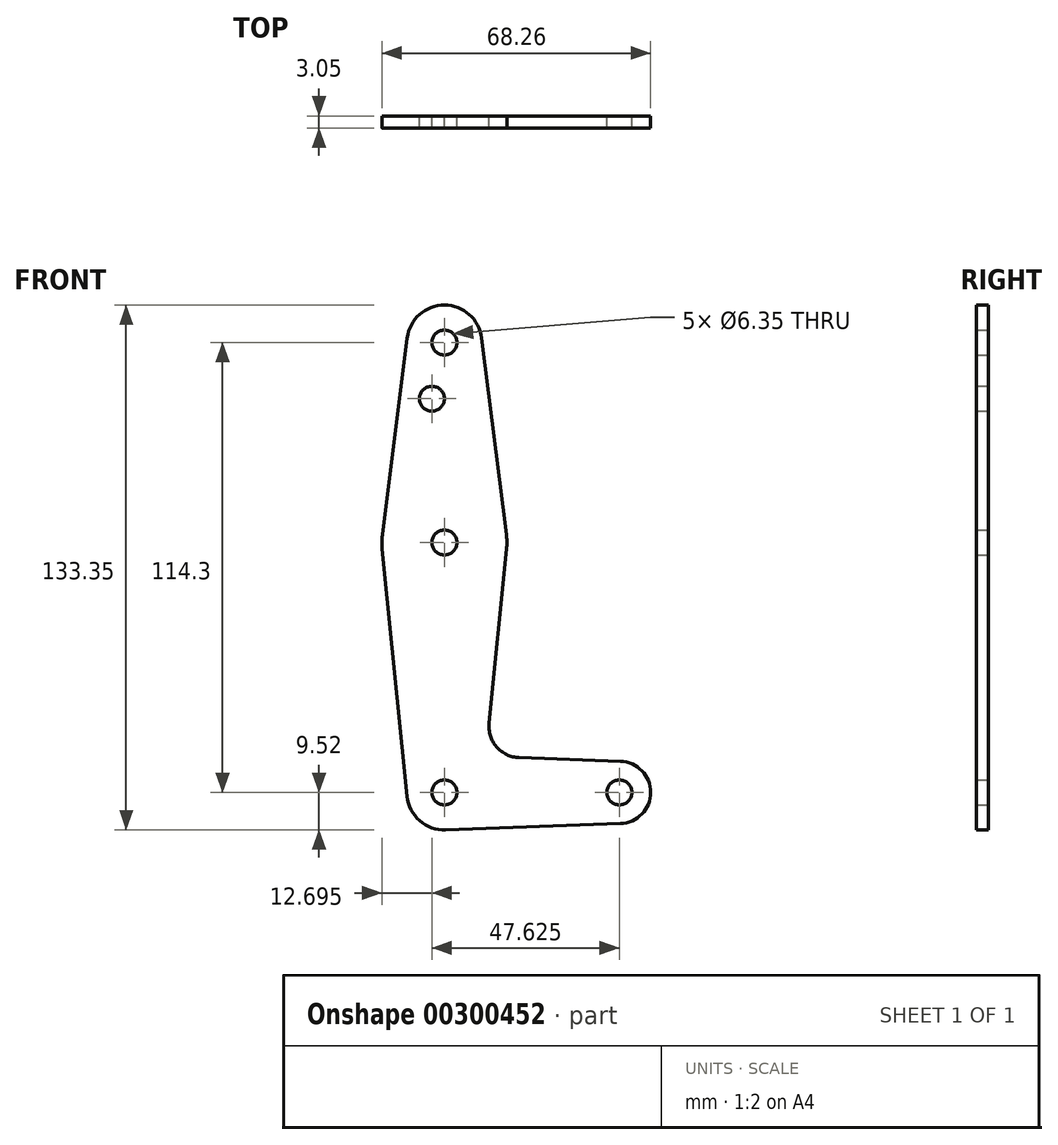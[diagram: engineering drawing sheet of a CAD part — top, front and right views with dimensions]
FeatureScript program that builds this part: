
annotation { "Feature Type Name" : "Feature", "Feature Type Description" : "" }
export const myFeature = defineFeature(function(context is Context, id is Id, definition is map)
    precondition{}
    {
        {
            var Q0;
            Q0=qCreatedBy(makeId("Front.planeOp"),FACE);
            var sketch = newSketch(context, id + "F0", { "sketchPlane" : qUnion([Q0])});
            skLineSegment(sketch, "E0", {"start": v(0, 114.3) * mm, "end": v(0, 0) * mm, "construction": true});
            skLineSegment(sketch, "E1", {"start": v(0, 0) * mm, "end": v(44.45, 0) * mm, "construction": true});
            skCircle(sketch, "E2", {"center": v(0, 63.5) * mm, "radius": 15.88 * mm});
            skCircle(sketch, "E3", {"center": v(0, 0) * mm, "radius": 9.53 * mm});
            skCircle(sketch, "E4", {"center": v(44.45, 0) * mm, "radius": 7.94 * mm});
            skCircle(sketch, "E5", {"center": v(0, 114.3) * mm, "radius": 9.53 * mm});
            skLineSegment(sketch, "E6", {"start": v(-9.45, 115.5) * mm, "end": v(-15.75, 65.48) * mm});
            skLineSegment(sketch, "E7", {"start": v(-15.8, 61.91) * mm, "end": v(-9.48, -0.95) * mm});
            skLineSegment(sketch, "E8", {"start": v(15.8, 61.91) * mm, "end": v(11.34, 17.6) * mm});
            skLineSegment(sketch, "E9", {"start": v(9.45, 115.5) * mm, "end": v(15.75, 65.48) * mm});
            skLineSegment(sketch, "E10", {"start": v(18.97, 8.85) * mm, "end": v(44.73, 7.93) * mm});
            skLineSegment(sketch, "E11", {"start": v(0.34, -9.52) * mm, "end": v(44.73, -7.93) * mm});
            skCircle(sketch, "E12", {"center": v(0, 114.3) * mm, "radius": 3.18 * mm});
            skCircle(sketch, "E13", {"center": v(-3.18, 100.03) * mm, "radius": 3.18 * mm});
            skCircle(sketch, "E14", {"center": v(0, 63.5) * mm, "radius": 3.18 * mm});
            skCircle(sketch, "E15", {"center": v(0, 0) * mm, "radius": 3.18 * mm});
            skCircle(sketch, "E16", {"center": v(44.45, 0) * mm, "radius": 3.18 * mm});
            skArc(sketch, "E17.filletArc", {"start": v(11.34, 17.6) * mm, "mid": v(13.26, 11.57) * mm, "end": v(18.97, 8.85) * mm});
            skSolve(sketch);
        }
        {
            var Q0;
            {var subQ1=sQuery(id+"F0.wireOp",EDGE,"E6");Q0=makeQuery(id+"F0.imprint","IMPRINT",FACE,{"disambiguationData":[TD([[makeQuery(id+"F0.imprint","IMPRINT",EDGE,{"derivedFrom":subQ1}),1.0]])]});}
            var Q1;
            Q1=makeQuery(id+"F0.imprint","IMPRINT",FACE,{"disambiguationData":[TD([[makeQuery(id+"F0.imprint","IMPRINT",EDGE,{"derivedFrom":sQuery(id+"F0.wireOp",EDGE,"E12")}),-1.0]])]});
            var Q2;
            Q2=makeQuery(id+"F0.imprint","IMPRINT",FACE,{"disambiguationData":[TD([[makeQuery(id+"F0.imprint","IMPRINT",EDGE,{"derivedFrom":sQuery(id+"F0.wireOp",EDGE,"E14")}),-1.0]])]});
            var Q3;
            {var subQ0=sQuery(id+"F0.wireOp",EDGE,"E7");Q3=makeQuery(id+"F0.imprint","IMPRINT",FACE,{"disambiguationData":[TD([[makeQuery(id+"F0.imprint","IMPRINT",EDGE,{"derivedFrom":subQ0}),1.0]])]});}
            var Q4;
            Q4=makeQuery(id+"F0.imprint","IMPRINT",FACE,{"disambiguationData":[TD([[makeQuery(id+"F0.imprint","IMPRINT",EDGE,{"derivedFrom":sQuery(id+"F0.wireOp",EDGE,"E15")}),-1.0]])]});
            var Q5;
            Q5=makeQuery(id+"F0.imprint","IMPRINT",FACE,{"disambiguationData":[TD([[makeQuery(id+"F0.imprint","IMPRINT",EDGE,{"derivedFrom":sQuery(id+"F0.wireOp",EDGE,"E16")}),-1.0]])]});
            extrude(context, id + "F1", {"entities" : qUnion([Q0, Q1, Q2, Q3, Q4, Q5]), "depth" : 3.05 * mm});
        }
    });
